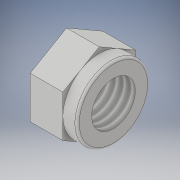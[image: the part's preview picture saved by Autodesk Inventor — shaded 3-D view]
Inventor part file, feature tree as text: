
AUTODESK INVENTOR PART (.ipt)
format: ipt  version: 2018 (Build 220112000, 112)  size: 133,632 bytes
history: native  units: in
note: dims shown in document units (in); Inventor stores cm internally (conversion verified against a paired STEP export)
features: extrude x2, sketch x2, fillet x1, thread x1
ambient origin geometry x8: Origin, YZ Plane, XZ Plane, XY Plane, X Axis, Y Axis, Z Axis, Center Point
bodies: Solid1 (feature_tree)
feature tree (6):
  extrude  "Extrusion1"  Depth=0.1575in
  extrude  "Extrusion2"  Depth=0.0512in TaperAngle=0.0deg
  fillet  "Fillet1"  Radius=0.0079in
  thread  "Thread1"  [1 undecoded]
  sketch  "Sketch1"  dims[d0=0.3031in d1=0.1575in]
  sketch  "Sketch2"  dims[d2=0.1181in d3=0.0in d4=0.0512in d5=0.0in d6=0.0079in d7=0.3937in d8=0.0in]
note: 1 required parameter value undecoded (feature->parameter linkage not recoverable at this tier; creation-order binding heuristic only, values carry confidence <= 0.55)
